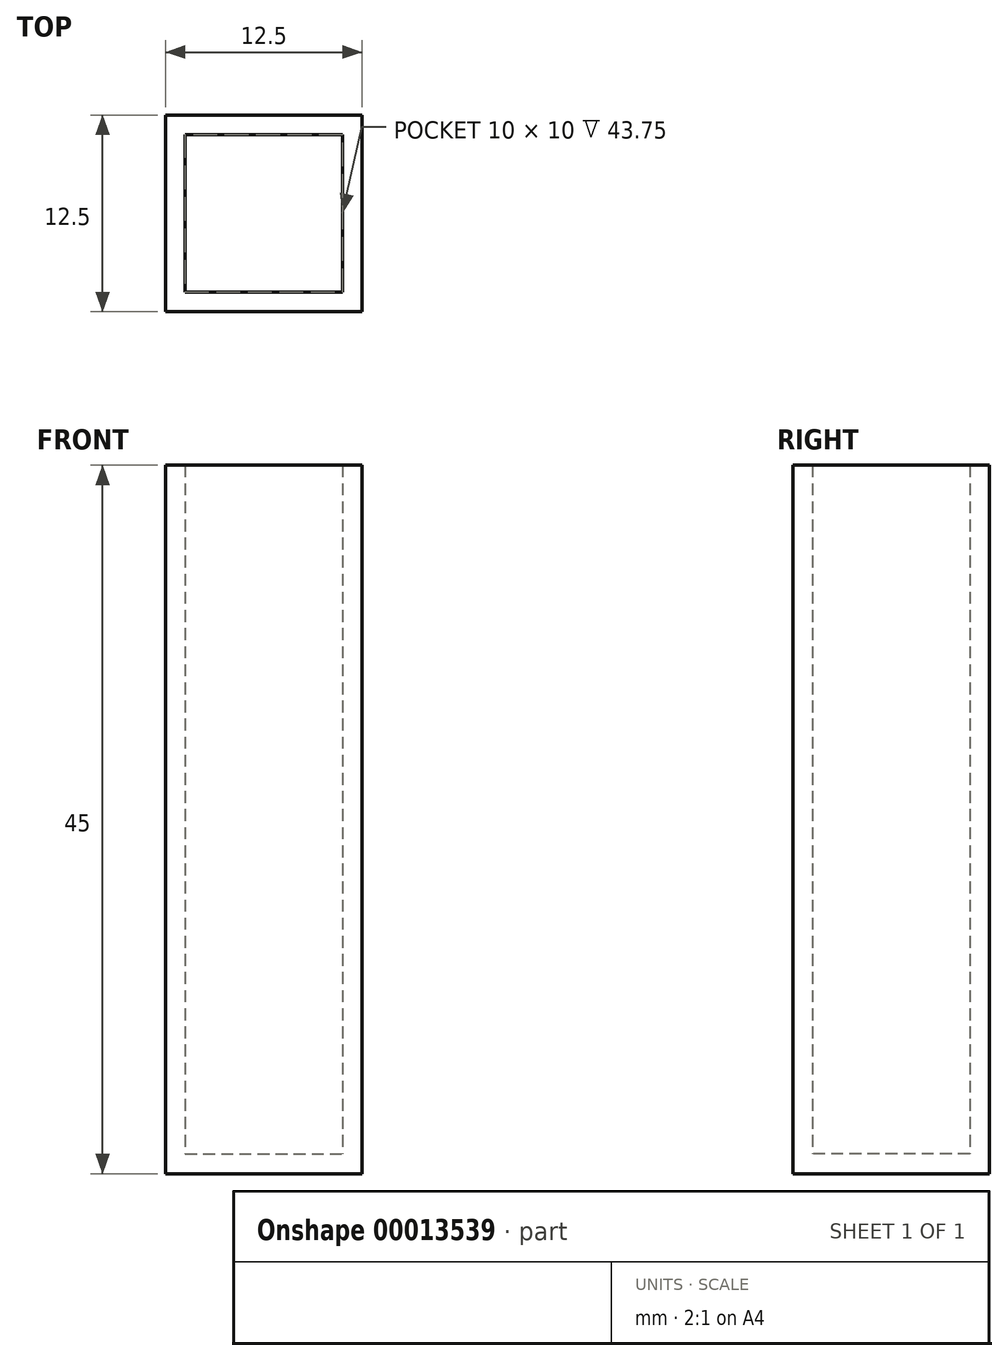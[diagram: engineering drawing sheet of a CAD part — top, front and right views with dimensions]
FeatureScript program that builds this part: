
annotation { "Feature Type Name" : "Feature", "Feature Type Description" : "" }
export const myFeature = defineFeature(function(context is Context, id is Id, definition is map)
    precondition{}
    {
        {
            var Q0;
            Q0=qCreatedBy(makeId("Top.planeOp"),FACE);
            var sketch = newSketch(context, id + "F0", { "sketchPlane" : qUnion([Q0])});
            skLineSegment(sketch, "E0.rect.bottom", {"start": v(6.25, 6.25) * mm, "end": v(-6.25, 6.25) * mm});
            skLineSegment(sketch, "E0.rect.top", {"start": v(6.25, -6.25) * mm, "end": v(-6.25, -6.25) * mm});
            skLineSegment(sketch, "E0.rect.left", {"start": v(6.25, 6.25) * mm, "end": v(6.25, -6.25) * mm});
            skLineSegment(sketch, "E0.rect.right", {"start": v(-6.25, 6.25) * mm, "end": v(-6.25, -6.25) * mm});
            skPoint(sketch, "E0.rect.middle", {"position": v(0, 0) * mm});
            skLineSegment(sketch, "E1.rect.bottom", {"start": v(5, -5) * mm, "end": v(-5, -5) * mm});
            skLineSegment(sketch, "E1.rect.top", {"start": v(5, 5) * mm, "end": v(-5, 5) * mm});
            skLineSegment(sketch, "E1.rect.left", {"start": v(5, -5) * mm, "end": v(5, 5) * mm});
            skLineSegment(sketch, "E1.rect.right", {"start": v(-5, -5) * mm, "end": v(-5, 5) * mm});
            skSolve(sketch);
        }
        {
            var Q0;
            Q0 = qSketchRegion(id + "F0", true);
            extrude(context, id + "F1", {"entities" : qUnion([Q0]), "depth" : 45 * mm});
        }
        {
            var Q0;
            Q0=makeQuery(id+"F1.opExtrude","CAP_FACE",FACE,{"disambiguationData":[OSD([sQuery(id+"F0.wireOp",EDGE,"E0.rect.bottom"),sQuery(id+"F0.wireOp",EDGE,"E0.rect.top"),sQuery(id+"F0.wireOp",EDGE,"E0.rect.left"),sQuery(id+"F0.wireOp",EDGE,"E0.rect.right"),sQuery(id+"F0.wireOp",EDGE,"E1.rect.bottom"),sQuery(id+"F0.wireOp",EDGE,"E1.rect.top"),sQuery(id+"F0.wireOp",EDGE,"E1.rect.left"),sQuery(id+"F0.wireOp",EDGE,"E1.rect.right")])],"isStart":true});
            var sketch = newSketch(context, id + "F2", { "sketchPlane" : qUnion([Q0])});
            skLineSegment(sketch, "E2.rect.bottom", {"start": v(-6.25, -6.25) * mm, "end": v(6.25, -6.25) * mm});
            skLineSegment(sketch, "E2.rect.top", {"start": v(-6.25, 6.25) * mm, "end": v(6.25, 6.25) * mm});
            skLineSegment(sketch, "E2.rect.left", {"start": v(-6.25, -6.25) * mm, "end": v(-6.25, 6.25) * mm});
            skLineSegment(sketch, "E2.rect.right", {"start": v(6.25, -6.25) * mm, "end": v(6.25, 6.25) * mm});
            skPoint(sketch, "E2.rect.middle", {"position": v(0, 0) * mm});
            skSolve(sketch);
        }
        {
            var Q0;
            Q0 = qSketchRegion(id + "F2", true);
            extrude(context, id + "F3", {"entities" : qUnion([Q0]), "operationType" : NewBodyOperationType.ADD, "oppositeDirection" : true, "depth" : 1.25 * mm});
        }
    });
